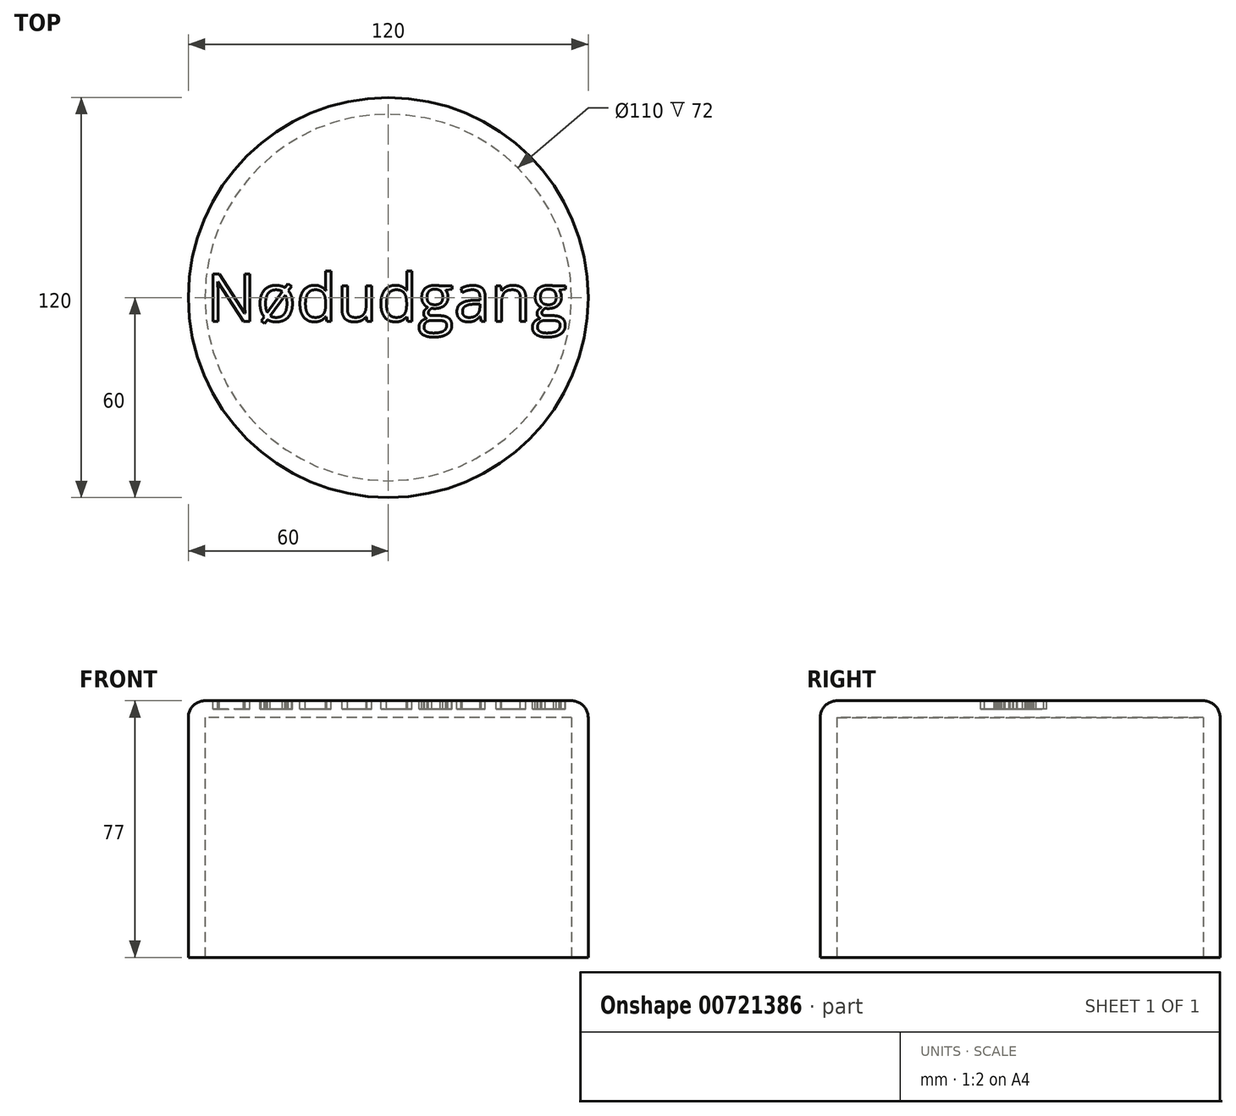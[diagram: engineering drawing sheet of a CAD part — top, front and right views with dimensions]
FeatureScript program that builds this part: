
annotation { "Feature Type Name" : "Feature", "Feature Type Description" : "" }
export const myFeature = defineFeature(function(context is Context, id is Id, definition is map)
    precondition{}
    {
        {
            var Q0;
            Q0=qCreatedBy(makeId("Top.planeOp"),FACE);
            var sketch = newSketch(context, id + "F0", { "sketchPlane" : qUnion([Q0])});
            skCircle(sketch, "E0", {"center": v(0, 0) * mm, "radius": 60 * mm});
            skSolve(sketch);
        }
        {
            var Q0;
            Q0 = qSketchRegion(id + "F0", true);
            extrude(context, id + "F1", {"entities" : qUnion([Q0]), "depth" : 77 * mm, "offsetDistance" : 25 * mm});
        }
        {
            var Q0;
            Q0=makeQuery(id+"F1.opExtrude","CAP_FACE",FACE,{"disambiguationData":[OSD([sQuery(id+"F0.wireOp",EDGE,"E0")])],"isStart":true});
            shell(context, id + "F2", {"entities" : qUnion([Q0]), "thickness" : 5 * mm});
        }
        {
            var Q0;
            Q0=makeQuery(id+"F1.opExtrude","CAP_EDGE",EDGE,{"disambiguationData":[OSD([sQuery(id+"F0.wireOp",EDGE,"E0")])],"isStart":false});
            fillet(context, id + "F3", {"entities" : qUnion([Q0]), "radius" : 5 * mm, "tangentPropagation" : true, "allowEdgeOverflow" : false});
        }
        {
            var Q0;
            Q0=makeQuery(id+"F1.opExtrude","CAP_FACE",FACE,{"disambiguationData":[OSD([sQuery(id+"F0.wireOp",EDGE,"E0")])],"isStart":false});
            var sketch = newSketch(context, id + "F4", { "sketchPlane" : qUnion([Q0])});
            skText(sketch, "E1", { "text": "Nødudgang", "fontName": "OpenSans-Regular.ttf"});
            const initialGuessF4  = {"E1": [-0.05454, -0.00713, 1, 0, 0.01427]};
            skSetInitialGuess(sketch, initialGuessF4);
            skSolve(sketch);
        }
        {
            var Q0;
            Q0 = qSketchRegion(id + "F4", true);
            extrude(context, id + "F5", {"entities" : qUnion([Q0]), "operationType" : NewBodyOperationType.REMOVE, "oppositeDirection" : true, "depth" : 2.5 * mm, "offsetDistance" : 25 * mm});
        }
    });
